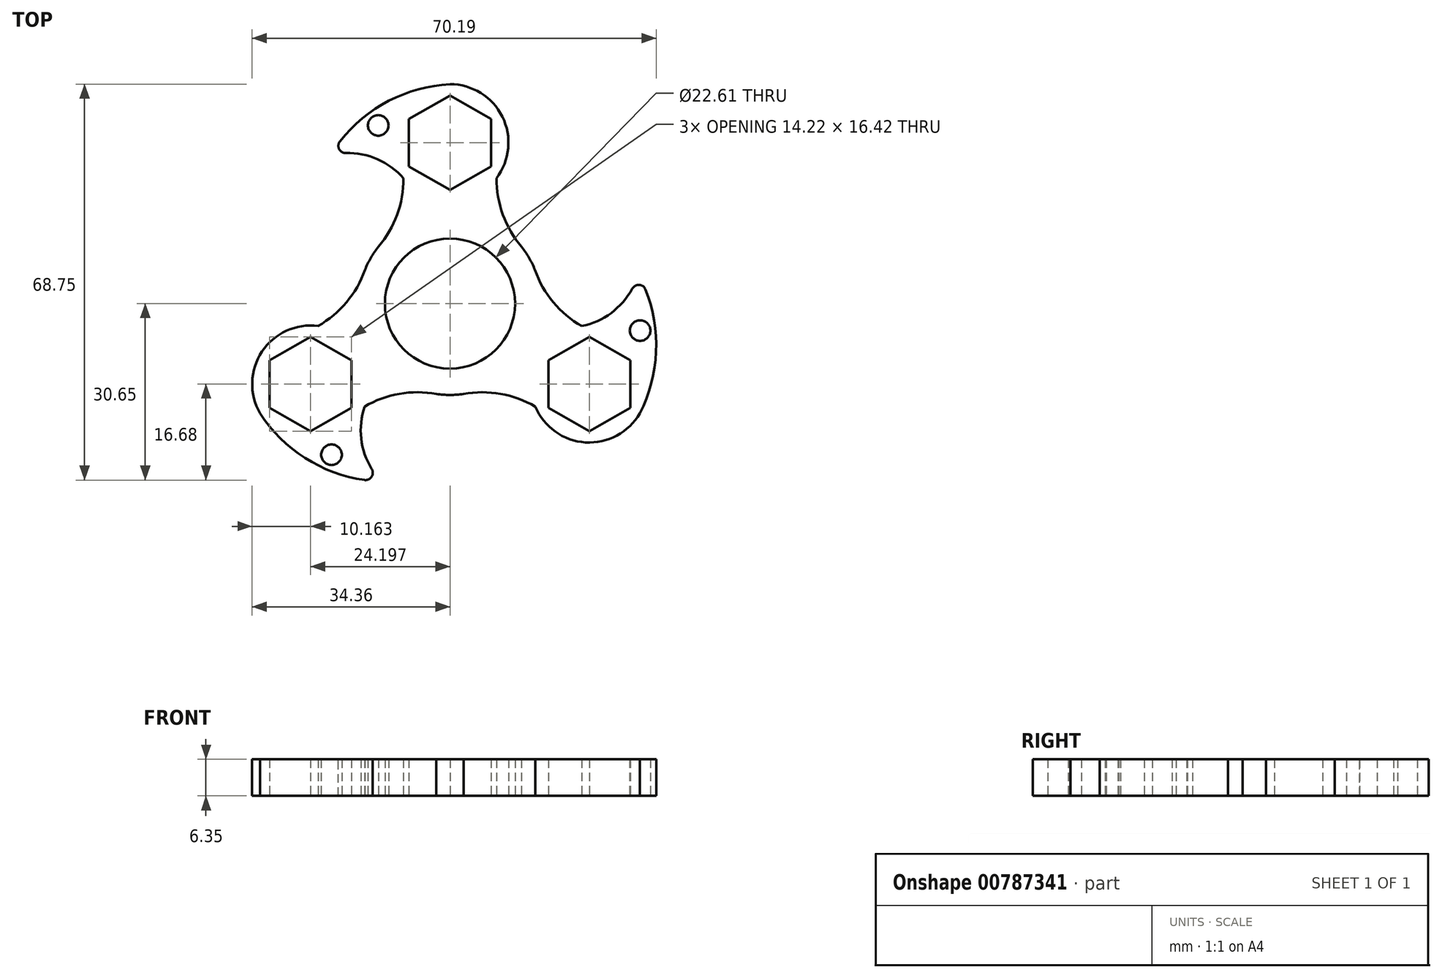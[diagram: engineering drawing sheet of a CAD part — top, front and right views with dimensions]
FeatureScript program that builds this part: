
annotation { "Feature Type Name" : "Feature", "Feature Type Description" : "" }
export const myFeature = defineFeature(function(context is Context, id is Id, definition is map)
    precondition{}
    {
        {
            var Q0;
            Q0=qCreatedBy(makeId("Top.planeOp"),FACE);
            var sketch = newSketch(context, id + "F0", { "sketchPlane" : qUnion([Q0])});
            skCircle(sketch, "E0", {"center": v(0, 0) * mm, "radius": 38.1 * mm});
            skCircle(sketch, "E1", {"center": v(0, 0) * mm, "radius": 11.3 * mm});
            skCircle(sketch, "E2.cCircle", {"center": v(0, 27.94) * mm, "radius": 8.21 * mm, "construction": true});
            skLineSegment(sketch, "E2.0", {"start": v(0, 36.15) * mm, "end": v(7.11, 32.05) * mm});
            skLineSegment(sketch, "E2.1", {"start": v(7.11, 32.05) * mm, "end": v(7.11, 23.83) * mm});
            skLineSegment(sketch, "E2.2", {"start": v(7.11, 23.83) * mm, "end": v(0, 19.73) * mm});
            skLineSegment(sketch, "E2.3", {"start": v(0, 19.73) * mm, "end": v(-7.11, 23.83) * mm});
            skLineSegment(sketch, "E2.4", {"start": v(-7.11, 23.83) * mm, "end": v(-7.11, 32.05) * mm});
            skLineSegment(sketch, "E2.5", {"start": v(-7.11, 32.05) * mm, "end": v(0, 36.15) * mm});
            skCircle(sketch, "E3", {"center": v(0, 27.94) * mm, "radius": 10.16 * mm});
            skCircle(sketch, "E4", {"center": v(0, 0) * mm, "radius": 15.88 * mm});
            skArc(sketch, "E5", {"start": v(8.08, 21.78) * mm, "mid": v(9.19, 15.44) * mm, "end": v(12.42, 9.88) * mm});
            skPoint(sketch, "E5.startSnap0", {"position": v(-3.56, 21.78) * mm});
            skArc(sketch, "E6", {"start": v(-12.42, 9.88) * mm, "mid": v(-9.18, 15.44) * mm, "end": v(-8.08, 21.78) * mm});
            skArc(sketch, "E7", {"start": v(0, 38.1) * mm, "mid": v(-11.92, 34.49) * mm, "end": v(-20.8, 25.76) * mm});
            skArc(sketch, "E8", {"start": v(-8.08, 21.78) * mm, "mid": v(-13.88, 25.55) * mm, "end": v(-20.8, 25.76) * mm});
            skCircle(sketch, "E9", {"center": v(-12.45, 30.94) * mm, "radius": 1.79 * mm});
            skArc(sketch, "E10.1.0", {"start": v(-14.82, -17.89) * mm, "mid": v(-15.18, -24.8) * mm, "end": v(-11.9, -30.9) * mm});
            skArc(sketch, "E10.1.1", {"start": v(-2.35, -15.7) * mm, "mid": v(-8.78, -15.67) * mm, "end": v(-14.82, -17.89) * mm});
            skArc(sketch, "E10.1.2", {"start": v(-33, -19.05) * mm, "mid": v(-23.9, -27.57) * mm, "end": v(-11.9, -30.9) * mm});
            skCircle(sketch, "E10.1.3", {"center": v(-24.2, -13.97) * mm, "radius": 10.16 * mm});
            skArc(sketch, "E10.1.4", {"start": v(-22.9, -3.9) * mm, "mid": v(-17.97, 0.23) * mm, "end": v(-14.77, 5.82) * mm});
            skCircle(sketch, "E10.1.5", {"center": v(-20.57, -26.26) * mm, "radius": 1.79 * mm});
            skLineSegment(sketch, "E10.1.6", {"start": v(-17.08, -18.08) * mm, "end": v(-24.2, -22.18) * mm});
            skLineSegment(sketch, "E10.1.7", {"start": v(-24.2, -22.18) * mm, "end": v(-31.3, -18.08) * mm});
            skLineSegment(sketch, "E10.1.8", {"start": v(-31.3, -18.08) * mm, "end": v(-31.3, -9.86) * mm});
            skLineSegment(sketch, "E10.1.9", {"start": v(-31.3, -9.86) * mm, "end": v(-24.2, -5.76) * mm});
            skLineSegment(sketch, "E10.1.10", {"start": v(-24.2, -5.76) * mm, "end": v(-17.08, -9.86) * mm});
            skLineSegment(sketch, "E10.1.11", {"start": v(-17.08, -9.86) * mm, "end": v(-17.08, -18.08) * mm});
            skArc(sketch, "E10.2.0", {"start": v(22.9, -3.9) * mm, "mid": v(29.07, -0.75) * mm, "end": v(32.7, 5.14) * mm});
            skArc(sketch, "E10.2.1", {"start": v(14.77, 5.82) * mm, "mid": v(17.96, 0.23) * mm, "end": v(22.9, -3.9) * mm});
            skArc(sketch, "E10.2.2", {"start": v(33, -19.05) * mm, "mid": v(35.83, -6.92) * mm, "end": v(32.7, 5.14) * mm});
            skCircle(sketch, "E10.2.3", {"center": v(24.2, -13.97) * mm, "radius": 10.16 * mm});
            skArc(sketch, "E10.2.4", {"start": v(14.82, -17.89) * mm, "mid": v(8.78, -15.68) * mm, "end": v(2.35, -15.7) * mm});
            skCircle(sketch, "E10.2.5", {"center": v(33.03, -4.69) * mm, "radius": 1.79 * mm});
            skLineSegment(sketch, "E10.2.6", {"start": v(24.2, -5.76) * mm, "end": v(31.3, -9.86) * mm});
            skLineSegment(sketch, "E10.2.7", {"start": v(31.3, -9.86) * mm, "end": v(31.3, -18.08) * mm});
            skLineSegment(sketch, "E10.2.8", {"start": v(31.3, -18.08) * mm, "end": v(24.2, -22.18) * mm});
            skLineSegment(sketch, "E10.2.9", {"start": v(24.2, -22.18) * mm, "end": v(17.08, -18.08) * mm});
            skLineSegment(sketch, "E10.2.10", {"start": v(17.08, -18.08) * mm, "end": v(17.08, -9.86) * mm});
            skLineSegment(sketch, "E10.2.11", {"start": v(17.08, -9.86) * mm, "end": v(24.2, -5.76) * mm});
            skSolve(sketch);
        }
        {
            var Q0;
            {var subQ0=sQuery(id+"F0.wireOp",EDGE,"E5");Q0=makeQuery(id+"F0.imprint","IMPRINT",FACE,{"disambiguationData":[TD([[makeQuery(id+"F0.imprint","IMPRINT",EDGE,{"derivedFrom":subQ0}),-1.0]])]});}
            var Q1;
            Q1=makeQuery(id+"F0.imprint","IMPRINT",FACE,{"disambiguationData":[TD([[makeQuery(id+"F0.imprint","IMPRINT",EDGE,{"derivedFrom":sQuery(id+"F0.wireOp",EDGE,"E2.0")}),1.0]])]});
            var Q2;
            {var subQ0=sQuery(id+"F0.wireOp",EDGE,"E8");Q2=makeQuery(id+"F0.imprint","IMPRINT",FACE,{"disambiguationData":[TD([[makeQuery(id+"F0.imprint","IMPRINT",EDGE,{"derivedFrom":subQ0}),-1.0]])]});}
            var Q3;
            Q3=makeQuery(id+"F0.imprint","IMPRINT",FACE,{"disambiguationData":[TD([[makeQuery(id+"F0.imprint","IMPRINT",EDGE,{"derivedFrom":sQuery(id+"F0.wireOp",EDGE,"E1")}),-1.0]])]});
            var Q4;
            Q4=makeQuery(id+"F0.imprint","IMPRINT",FACE,{"disambiguationData":[TD([[makeQuery(id+"F0.imprint","IMPRINT",EDGE,{"derivedFrom":sQuery(id+"F0.wireOp",EDGE,"E10.1.6")}),1.0]])]});
            var Q5;
            {var subQ0=sQuery(id+"F0.wireOp",EDGE,"E10.1.1");Q5=makeQuery(id+"F0.imprint","IMPRINT",FACE,{"disambiguationData":[TD([[makeQuery(id+"F0.imprint","IMPRINT",EDGE,{"derivedFrom":subQ0}),-1.0]])]});}
            var Q6;
            {var subQ1=sQuery(id+"F0.wireOp",EDGE,"E10.1.0");Q6=makeQuery(id+"F0.imprint","IMPRINT",FACE,{"disambiguationData":[TD([[makeQuery(id+"F0.imprint","IMPRINT",EDGE,{"derivedFrom":subQ1}),-1.0]])]});}
            var Q7;
            {var subQ0=sQuery(id+"F0.wireOp",EDGE,"E10.2.1");Q7=makeQuery(id+"F0.imprint","IMPRINT",FACE,{"disambiguationData":[TD([[makeQuery(id+"F0.imprint","IMPRINT",EDGE,{"derivedFrom":subQ0}),-1.0]])]});}
            var Q8;
            Q8=makeQuery(id+"F0.imprint","IMPRINT",FACE,{"disambiguationData":[TD([[makeQuery(id+"F0.imprint","IMPRINT",EDGE,{"derivedFrom":sQuery(id+"F0.wireOp",EDGE,"E10.2.6")}),1.0]])]});
            var Q9;
            {var subQ1=sQuery(id+"F0.wireOp",EDGE,"E10.2.0");Q9=makeQuery(id+"F0.imprint","IMPRINT",FACE,{"disambiguationData":[TD([[makeQuery(id+"F0.imprint","IMPRINT",EDGE,{"derivedFrom":subQ1}),-1.0]])]});}
            extrude(context, id + "F1", {"entities" : qUnion([Q0, Q1, Q2, Q3, Q4, Q5, Q6, Q7, Q8, Q9]), "depth" : 6.35 * mm, "offsetDistance" : 25.4 * mm});
        }
        {
            var Q0;
            Q0=makeQuery(id+"F1.opExtrude","SWEPT_EDGE",EDGE,{"disambiguationData":[OSD([sQuery(id+"F0.wireOp",EDGE,"E7"),sQuery(id+"F0.wireOp",EDGE,"E8")])]});
            var Q1;
            Q1=makeQuery(id+"F1.opExtrude","SWEPT_EDGE",EDGE,{"disambiguationData":[OSD([sQuery(id+"F0.wireOp",EDGE,"E10.1.0"),sQuery(id+"F0.wireOp",EDGE,"E10.1.2")])]});
            var Q2;
            Q2=makeQuery(id+"F1.opExtrude","SWEPT_EDGE",EDGE,{"disambiguationData":[OSD([sQuery(id+"F0.wireOp",EDGE,"E10.2.0"),sQuery(id+"F0.wireOp",EDGE,"E10.2.2")])]});
            fillet(context, id + "F2", {"entities" : qUnion([Q0, Q1, Q2]), "radius" : 1.27 * mm, "tangentPropagation" : true, "allowEdgeOverflow" : false});
        }
    });
